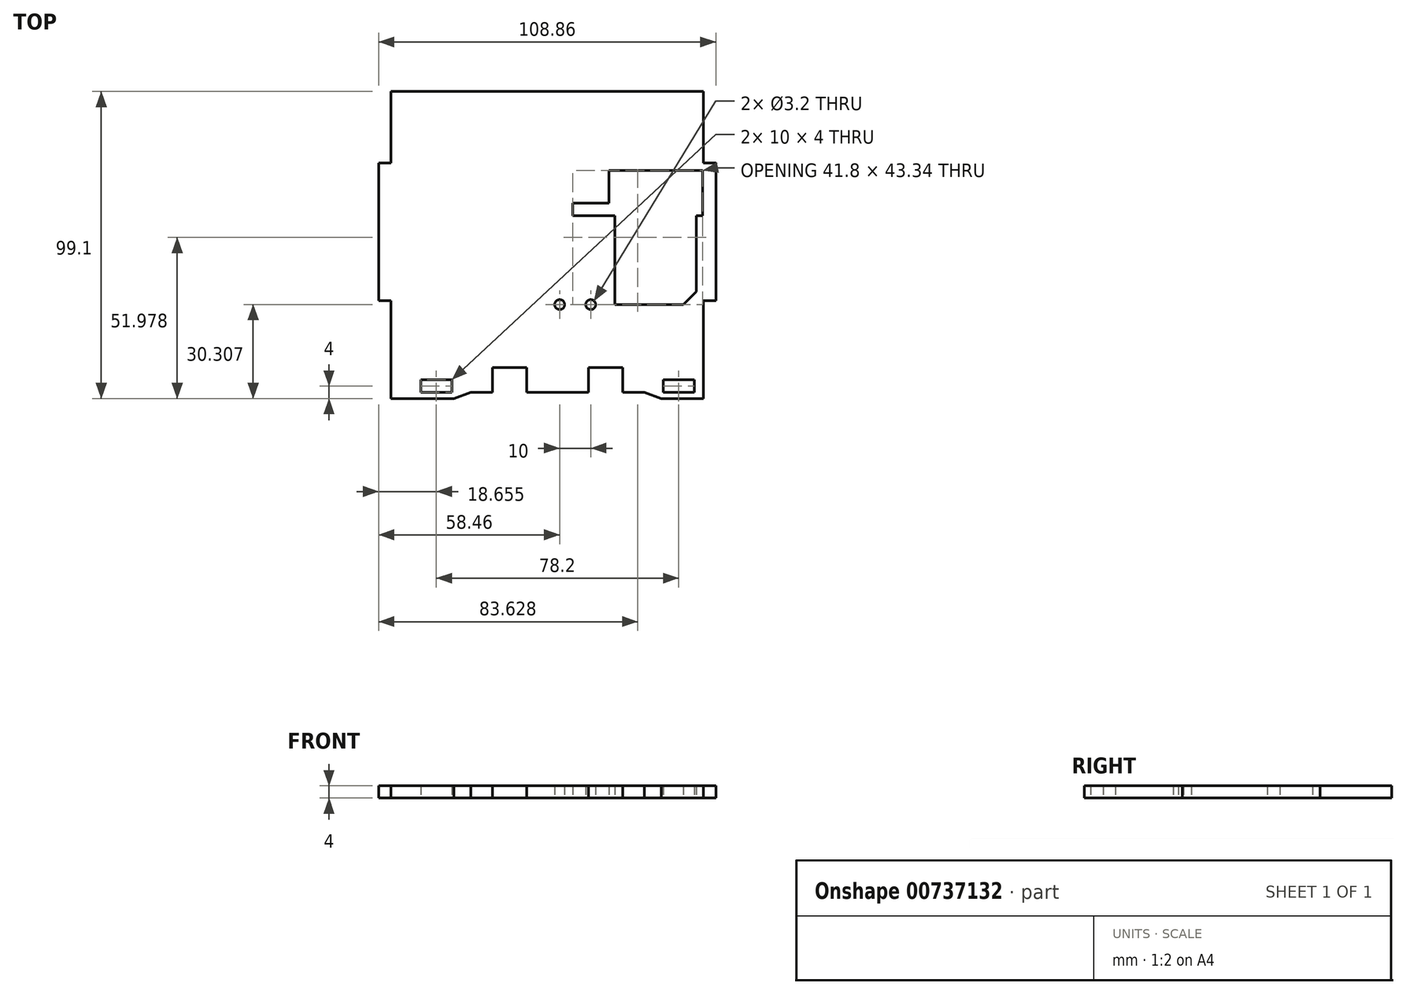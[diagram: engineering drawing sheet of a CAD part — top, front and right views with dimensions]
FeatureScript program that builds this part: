
annotation { "Feature Type Name" : "Feature", "Feature Type Description" : "" }
export const myFeature = defineFeature(function(context is Context, id is Id, definition is map)
    precondition{}
    {
        {
            var Q0;
            Q0=qCreatedBy(makeId("Top.planeOp"),FACE);
            var sketch = newSketch(context, id + "F0", { "sketchPlane" : qUnion([Q0])});
            skLineSegment(sketch, "E0.bottom", {"start": v(-50.43, 49.55) * mm, "end": v(50.42, 49.55) * mm});
            skLineSegment(sketch, "E0.top", {"start": v(-50.42, -49.55) * mm, "end": v(-30.17, -49.55) * mm});
            skLineSegment(sketch, "E0.left", {"start": v(-50.43, 49.55) * mm, "end": v(-50.43, 26.5) * mm});
            skLineSegment(sketch, "E0.right", {"start": v(50.42, 49.55) * mm, "end": v(50.42, 26.5) * mm});
            skPoint(sketch, "E0.middle", {"position": v(0, 0) * mm});
            skLineSegment(sketch, "E1", {"start": v(50.42, 26.5) * mm, "end": v(54.42, 26.5) * mm});
            skLineSegment(sketch, "E2", {"start": v(54.42, 26.5) * mm, "end": v(54.43, -18) * mm});
            skLineSegment(sketch, "E3", {"start": v(54.42, -18) * mm, "end": v(50.43, -18) * mm});
            skLineSegment(sketch, "E4", {"start": v(50.42, 26.5) * mm, "end": v(50.42, -18) * mm, "construction": true});
            skLineSegment(sketch, "E5", {"start": v(-50.43, 26.5) * mm, "end": v(-54.43, 26.5) * mm});
            skLineSegment(sketch, "E6", {"start": v(-54.43, 26.5) * mm, "end": v(-54.42, -18) * mm});
            skLineSegment(sketch, "E7", {"start": v(-54.42, -18) * mm, "end": v(-50.42, -18) * mm});
            skLineSegment(sketch, "E8", {"start": v(-50.43, 26.5) * mm, "end": v(-50.42, -18) * mm, "construction": true});
            skLineSegment(sketch, "E9", {"start": v(-50.42, -18) * mm, "end": v(-50.42, -49.55) * mm});
            skLineSegment(sketch, "E10", {"start": v(50.42, -18) * mm, "end": v(50.42, -49.55) * mm});
            skLineSegment(sketch, "E11", {"start": v(19.9, 24.1) * mm, "end": v(19.9, 13.5) * mm});
            skLineSegment(sketch, "E12", {"start": v(19.9, 13.5) * mm, "end": v(8.3, 13.5) * mm});
            skLineSegment(sketch, "E13", {"start": v(8.3, 13.5) * mm, "end": v(8.3, 9.5) * mm});
            skLineSegment(sketch, "E14", {"start": v(8.3, 9.5) * mm, "end": v(21.88, 9.5) * mm});
            skLineSegment(sketch, "E15", {"start": v(21.88, 9.5) * mm, "end": v(21.88, -19.24) * mm});
            skLineSegment(sketch, "E16", {"start": v(21.88, -19.24) * mm, "end": v(43.88, -19.24) * mm});
            skLineSegment(sketch, "E17", {"start": v(43.88, -19.24) * mm, "end": v(48.12, -15) * mm});
            skLineSegment(sketch, "E18", {"start": v(48.12, -15) * mm, "end": v(48.12, 9.5) * mm});
            skLineSegment(sketch, "E19", {"start": v(48.12, 9.5) * mm, "end": v(50.1, 9.5) * mm});
            skLineSegment(sketch, "E20", {"start": v(50.1, 9.5) * mm, "end": v(50.1, 24.1) * mm});
            skLineSegment(sketch, "E21", {"start": v(50.1, 24.1) * mm, "end": v(19.9, 24.1) * mm});
            skCircle(sketch, "E22", {"center": v(14.03, -19.24) * mm, "radius": 1.6 * mm});
            skCircle(sketch, "E23", {"center": v(4.03, -19.24) * mm, "radius": 1.6 * mm});
            skLineSegment(sketch, "E24.bottom", {"start": v(37.43, -43.55) * mm, "end": v(47.43, -43.55) * mm});
            skLineSegment(sketch, "E24.top", {"start": v(37.43, -47.55) * mm, "end": v(47.43, -47.55) * mm});
            skLineSegment(sketch, "E24.left", {"start": v(37.43, -43.55) * mm, "end": v(37.43, -47.55) * mm});
            skLineSegment(sketch, "E24.right", {"start": v(47.43, -43.55) * mm, "end": v(47.43, -47.55) * mm});
            skLineSegment(sketch, "E25", {"start": v(36.82, -49.55) * mm, "end": v(50.43, -49.55) * mm});
            skLineSegment(sketch, "E26", {"start": v(31.32, -47.55) * mm, "end": v(36.82, -49.55) * mm});
            skLineSegment(sketch, "E27", {"start": v(31.32, -47.55) * mm, "end": v(24.32, -47.55) * mm});
            skLineSegment(sketch, "E28", {"start": v(24.32, -47.55) * mm, "end": v(24.32, -39.55) * mm});
            skLineSegment(sketch, "E29", {"start": v(24.32, -39.55) * mm, "end": v(13.32, -39.55) * mm});
            skLineSegment(sketch, "E30", {"start": v(13.32, -39.55) * mm, "end": v(13.32, -47.55) * mm});
            skLineSegment(sketch, "E31", {"start": v(13.32, -47.55) * mm, "end": v(-6.68, -47.55) * mm});
            skLineSegment(sketch, "E32", {"start": v(-6.68, -47.55) * mm, "end": v(-6.68, -39.55) * mm});
            skLineSegment(sketch, "E33", {"start": v(-6.68, -39.55) * mm, "end": v(-17.68, -39.55) * mm});
            skLineSegment(sketch, "E34", {"start": v(-17.68, -39.55) * mm, "end": v(-17.68, -47.55) * mm});
            skLineSegment(sketch, "E35", {"start": v(-17.68, -47.55) * mm, "end": v(-24.68, -47.55) * mm});
            skLineSegment(sketch, "E36", {"start": v(-24.68, -47.55) * mm, "end": v(-30.17, -49.55) * mm});
            skLineSegment(sketch, "E37.bottom", {"start": v(-40.77, -43.55) * mm, "end": v(-30.77, -43.55) * mm});
            skLineSegment(sketch, "E37.top", {"start": v(-40.77, -47.55) * mm, "end": v(-30.77, -47.55) * mm});
            skLineSegment(sketch, "E37.left", {"start": v(-40.77, -43.55) * mm, "end": v(-40.77, -47.55) * mm});
            skLineSegment(sketch, "E37.right", {"start": v(-30.77, -43.55) * mm, "end": v(-30.77, -47.55) * mm});
            skSolve(sketch);
        }
        {
            var Q0;
            Q0=makeQuery(id+"F0.imprint","IMPRINT",FACE,{"disambiguationData":[TD([[makeQuery(id+"F0.imprint","IMPRINT",EDGE,{"derivedFrom":sQuery(id+"F0.wireOp",EDGE,"E0.bottom")}),-1.0]])]});
            extrude(context, id + "F1", {"entities" : qUnion([Q0]), "depth" : 4 * mm, "offsetDistance" : 25 * mm});
        }
    });
